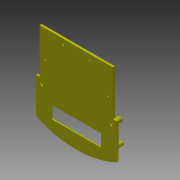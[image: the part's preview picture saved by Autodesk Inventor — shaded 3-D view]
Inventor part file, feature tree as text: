
AUTODESK INVENTOR PART (.ipt)
format: ipt  version: 2015 (Build 190159000, 159)  size: 544,768 bytes
history: native  units: mm
features: extrude x20, sketch x15, fillet x10, other x1, revolve x1
ambient origin geometry x8: Origin, YZ Plane, XZ Plane, XY Plane, X Axis, Y Axis, Z Axis, Center Point
bodies: Body1 (feature_tree)
feature tree (47):
  other  "Sólido1"
  sketch  "Boceto1"  dims[d0=37.0mm d1=57.0mm]
  extrude  "Extrusión1"  Depth=57.0mm
  extrude  "Extrusión2"  Depth=10.0mm
  extrude  "Extrusión3"  Depth=57.0mm
  sketch  "Boceto3"  dims[d4=20.0mm d5=57.0mm]
  extrude  "Extrusión4"  Depth=79.0mm
  extrude  "Extrusión5"  Depth=36.0mm
  extrude  "Extrusión6"  Depth=72.0mm
  extrude  "Extrusión7"  Depth=13.0mm
  fillet  "Empalme2"  Radius=3.0mm
  fillet  "Empalme3"  Radius=40.0mm
  fillet  "Empalme4"  Radius=13.0mm
  fillet  "Empalme5"  Radius=1111.0mm
  extrude  "Extrusión10"  Depth=5.0mm TaperAngle=0.0deg
  fillet  "Empalme10"  Radius=111.0mm
  sketch  "Boceto6"  dims[d6=37.0mm d7=79.0mm]
  extrude  "Extrusión11"  Depth=3.0mm
  extrude  "Extrusión12"  Depth=3.0mm
  fillet  "Empalme11"  Radius=2.0mm
  fillet  "Empalme12"  Radius=3.0mm
  revolve  "Revolución1"  [1 undecoded]
  fillet  "Empalme13"  Radius=6.5mm
  extrude  "Extrusión14"  Depth=3.0mm TaperAngle=0.0deg
  extrude  "Extrusión15"  Depth=2.0mm
  extrude  "Extrusión16"  Depth=19.5mm
  extrude  "Extrusión17"  Depth=10.0mm
  extrude  "Extrusión19"  Depth=4.0mm
  extrude  "Extrusión20"  Depth=10.0mm TaperAngle=0.0deg
  extrude  "Extrusión21"  Depth=8.0mm TaperAngle=0.0deg
  fillet  "Empalme14"  Radius=20.0mm
  extrude  "Extrusión22"  Depth=4.0mm
  extrude  "Extrusión23"  Depth=4.0mm
  fillet  "Empalme15"  Radius=140.0mm
  extrude  "Extrusión24"  Depth=4.0mm
  sketch  "Boceto2"  dims[d2=20.0mm d3=10.0mm]
  sketch  "Boceto8"  dims[d8=6.0mm d9=36.0mm]
  sketch  "Boceto9"  dims[d10=7.0mm d11=72.0mm]
  sketch  "Boceto10"  dims[d16=290.0mm d17=5.0mm d18=3.0mm d19=0.0mm d20=40.0mm d21=0.0mm d22=13.0mm d23=1111.0mm d24=0.0mm]
  sketch  "Boceto11"  dims[d25=5.0mm d26=0.0mm d27=5.0mm d28=0.0mm d29=111.0mm d30=0.0mm]
  sketch  "Boceto12"  dims[d31=3.0mm d32=0.0mm d41=1.0mm]
  sketch  "Boceto14"  dims[d42=5.0mm d43=5.0mm d44=2.0mm d47=3.0mm d48=0.0mm]
  sketch  "Boceto15"  dims[d51=1.0mm d53=2.5mm d54=6.5mm]
  sketch  "Boceto16"  dims[d55=3.0mm d56=0.0mm d57=3.0mm d58=0.0mm]
  sketch  "Boceto17"  dims[d59=1.0mm d60=2.0mm]
  sketch  "Boceto18"  dims[d63=19.5mm d64=19.5mm]
  sketch  "Boceto19"  dims[d65=180.0deg d66=10.0mm d67=270.0mm d68=10.0mm d69=0.0mm d70=292.0mm d71=300.0mm d72=270.0mm d73=10.0mm d74=6.0mm d75=3.0mm d76=0.5mm d77=35.0mm d78=3.0mm d79=0.5mm d80=6.0mm d81=35.0mm d82=40.0mm d84=360.0deg d86=8.0mm d87=0.0mm d88=20.0mm d89=75.0mm d90=40.0mm d91=140.0mm d92=20.0mm d93=20.0mm d94=111.0mm d95=0.0mm d96=5.0mm d97=70.0mm d98=5.0mm d99=70.0mm d100=5.0mm d101=10.0mm d102=0.0mm d110=3.0mm d111=3.0mm d112=3.0mm d113=3.0mm d114=10.0mm d115=0.0mm d116=0.3mm d117=10.0mm d118=0.0mm d119=8.0mm d120=16.0mm d121=10.0mm d122=0.0mm d123=4.0mm d124=4.2mm d125=111.0mm d126=0.0mm d127=8.0mm d128=16.0mm d129=10.0mm d130=0.0mm d131=4.0mm d132=4.2mm d133=111.0mm d134=0.0mm]
note: 1 required parameter value undecoded (feature->parameter linkage not recoverable at this tier; creation-order binding heuristic only, values carry confidence <= 0.55)
